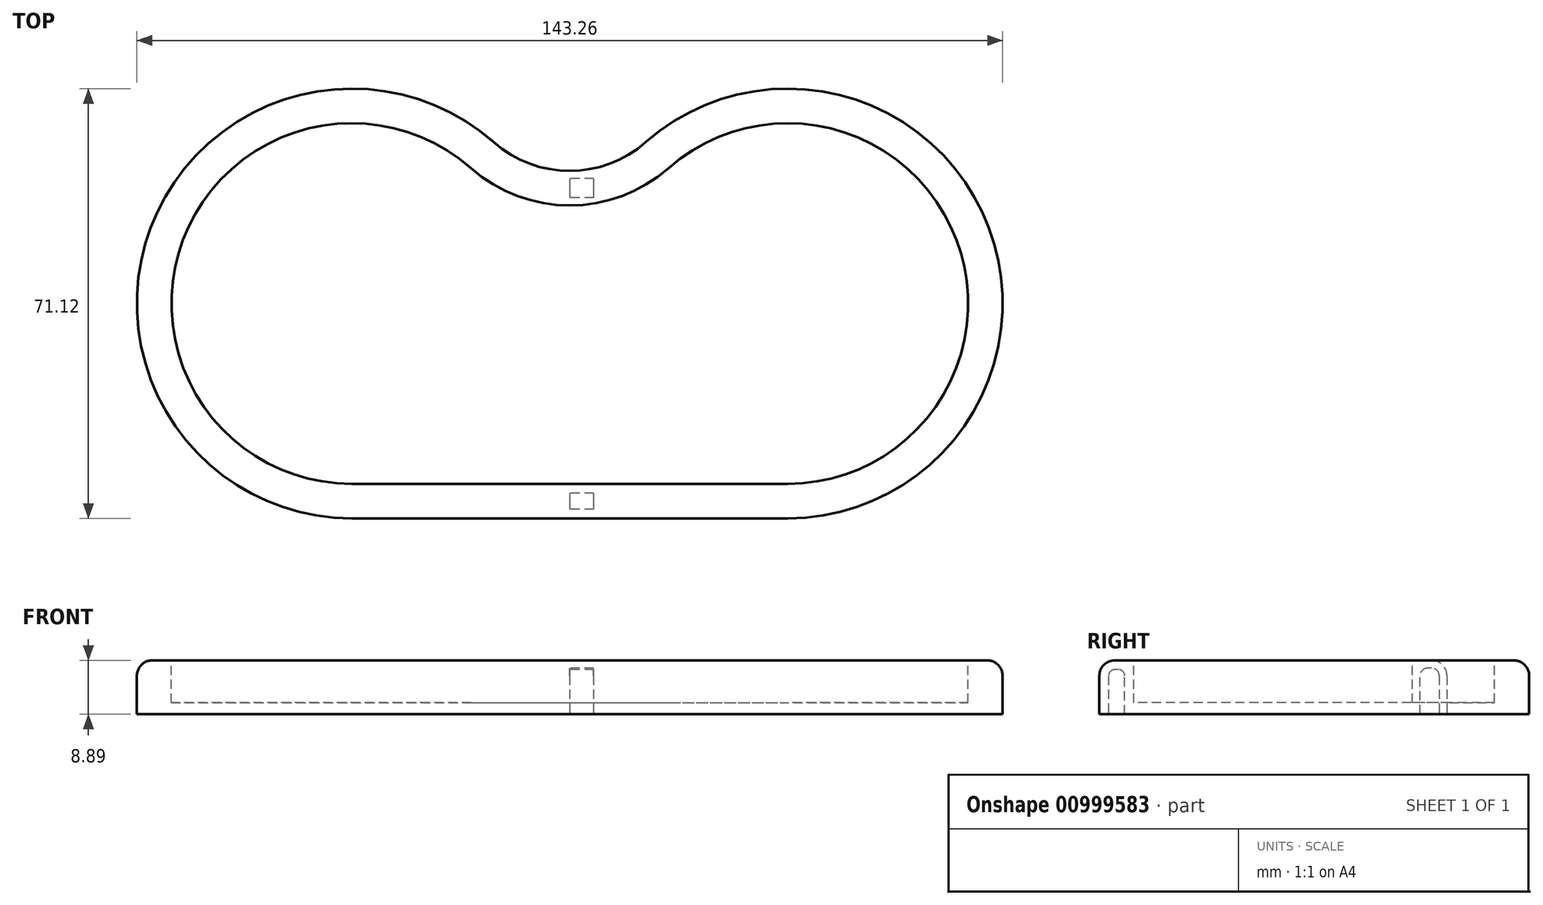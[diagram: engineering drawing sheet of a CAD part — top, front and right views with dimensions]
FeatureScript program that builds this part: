
annotation { "Feature Type Name" : "Feature", "Feature Type Description" : "" }
export const myFeature = defineFeature(function(context is Context, id is Id, definition is map)
    precondition{}
    {
        {
            var Q0;
            Q0=qCreatedBy(makeId("Top.planeOp"),FACE);
            var sketch = newSketch(context, id + "F0", { "sketchPlane" : qUnion([Q0])});
            skArc(sketch, "E0.0", {"start": v(-12.58, 29.6) * mm, "mid": v(-69.34, 15.46) * mm, "end": v(-36.07, -32.66) * mm});
            skLineSegment(sketch, "E1", {"start": v(-36.07, -32.66) * mm, "end": v(0, -32.66) * mm});
            skArc(sketch, "E2.filletArc", {"start": v(-12.58, 29.6) * mm, "mid": v(-6.72, 26.09) * mm, "end": v(0, 24.86) * mm});
            skLineSegment(sketch, "E3", {"start": v(0, 24.86) * mm, "end": v(0, -32.66) * mm});
            skSolve(sketch);
        }
        {
            var Q0;
            Q0 = qSketchRegion(id + "F0", true);
            extrude(context, id + "F1", {"entities" : qUnion([Q0]), "depth" : 8.9 * mm, "offsetDistance" : 25.4 * mm});
        }
        {
            var Q0;
            Q0=makeQuery(id+"F1.opExtrude","CAP_FACE",FACE,{"disambiguationData":[OSD([sQuery(id+"F0.wireOp",EDGE,"E0.0"),sQuery(id+"F0.wireOp",EDGE,"E1"),sQuery(id+"F0.wireOp",EDGE,"E2.filletArc"),sQuery(id+"F0.wireOp",EDGE,"E3")])],"isStart":false});
            var sketch = newSketch(context, id + "F2", { "sketchPlane" : qUnion([Q0])});
            skLineSegment(sketch, "E4.0", {"start": v(-36.07, -26.94) * mm, "end": v(0, -26.94) * mm});
            skArc(sketch, "E4.2", {"start": v(-16.36, 25.31) * mm, "mid": v(-8.74, 20.74) * mm, "end": v(0, 19.14) * mm});
            skLineSegment(sketch, "E5", {"start": v(0, 19.14) * mm, "end": v(0, -26.94) * mm});
            skArc(sketch, "E6", {"start": v(-16.36, 25.31) * mm, "mid": v(-64, 13.44) * mm, "end": v(-36.07, -26.94) * mm});
            skArc(sketch, "E7", {"start": v(-36.07, -26.94) * mm, "mid": v(-8.14, -7.63) * mm, "end": v(-16.36, 25.31) * mm, "construction": true});
            skSolve(sketch);
        }
        {
            var Q0;
            Q0 = qSketchRegion(id + "F2", true);
            extrude(context, id + "F3", {"entities" : qUnion([Q0]), "operationType" : NewBodyOperationType.REMOVE, "oppositeDirection" : true, "depth" : 7 * mm, "offsetDistance" : 25.4 * mm});
        }
        {
            var Q0;
            Q0=makeQuery(id+"F3.boolean.opBoolean","COPY",EDGE,{"derivedFrom":makeQuery(id+"F3.opExtrude","CAP_EDGE",EDGE,{"disambiguationData":[OSD([sQuery(id+"F2.wireOp",EDGE,"E4.2")])],"isStart":true})});
            var Q1;
            Q1=makeQuery(id+"F1.opExtrude","CAP_EDGE",EDGE,{"disambiguationData":[OSD([sQuery(id+"F0.wireOp",EDGE,"E2.filletArc")])],"isStart":false});
            fillet(context, id + "F4", {"entities" : qUnion([Q0, Q1]), "radius" : 2.54 * mm, "tangentPropagation" : true, "allowEdgeOverflow" : false});
        }
        {
            var Q0;
            Q0=makeQuery(id+"F1.opExtrude","SWEPT_FACE",FACE,{"disambiguationData":[OSD([sQuery(id+"F0.wireOp",EDGE,"E3")])]});
            var sketch = newSketch(context, id + "F5", { "sketchPlane" : qUnion([Q0])});
            skLineSegment(sketch, "E8.0", {"start": v(-31.13, 6.35) * mm, "end": v(-31.13, 0) * mm});
            skLineSegment(sketch, "E8.1", {"start": v(-28.46, 0) * mm, "end": v(-28.46, 6.35) * mm});
            skArc(sketch, "E8.2", {"start": v(-28.46, 6.35) * mm, "mid": v(-28.76, 7.07) * mm, "end": v(-29.48, 7.37) * mm});
            skLineSegment(sketch, "E8.3", {"start": v(-29.48, 7.37) * mm, "end": v(-30.12, 7.37) * mm});
            skArc(sketch, "E8.4", {"start": v(-30.12, 7.37) * mm, "mid": v(-30.83, 7.07) * mm, "end": v(-31.13, 6.35) * mm});
            skLineSegment(sketch, "E9", {"start": v(-31.13, 0) * mm, "end": v(-28.46, 0) * mm});
            skLineSegment(sketch, "E10.0", {"start": v(23.59, 6.35) * mm, "end": v(23.59, 0) * mm});
            skLineSegment(sketch, "E10.1", {"start": v(20.41, 0) * mm, "end": v(20.41, 6.35) * mm});
            skArc(sketch, "E10.2", {"start": v(21.68, 7.62) * mm, "mid": v(20.79, 7.25) * mm, "end": v(20.41, 6.35) * mm});
            skLineSegment(sketch, "E10.3", {"start": v(22.32, 7.62) * mm, "end": v(21.68, 7.62) * mm});
            skArc(sketch, "E10.4", {"start": v(23.59, 6.35) * mm, "mid": v(23.22, 7.25) * mm, "end": v(22.32, 7.62) * mm});
            skLineSegment(sketch, "E11", {"start": v(20.41, 0) * mm, "end": v(23.59, 0) * mm});
            skSolve(sketch);
        }
        {
            var Q0;
            Q0=makeQuery(id+"F1.opExtrude","SWEPT_BODY",BODY,{"disambiguationData":[OSD([sQuery(id+"F0.wireOp",EDGE,"E0.0"),sQuery(id+"F0.wireOp",EDGE,"E1"),sQuery(id+"F0.wireOp",EDGE,"E2.filletArc"),sQuery(id+"F0.wireOp",EDGE,"E3")])]});
            var Q1;
            Q1=qCreatedBy(makeId("Right.planeOp"),FACE);
            mirror(context, id + "F6", {"entities" : qUnion([Q0]), "mirrorPlane" : qUnion([Q1])});
        }
        {
            var Q0;
            {var subQ15=sQuery(id+"F5.wireOp",EDGE,"E8.0");Q0=makeQuery(id+"F5.imprint","IMPRINT",FACE,{"disambiguationData":[TD([[makeQuery(id+"F5.imprint","IMPRINT",EDGE,{"derivedFrom":subQ15}),-1.0]])]});}
            var sketch = newSketch(context, id + "F7", { "sketchPlane" : qUnion([Q0])});
            skArc(sketch, "E12.0", {"start": v(-30.12, 7.32) * mm, "mid": v(-30.8, 7.03) * mm, "end": v(-31.08, 6.35) * mm});
            skLineSegment(sketch, "E12.2", {"start": v(-28.52, 0) * mm, "end": v(-28.52, 6.35) * mm});
            skLineSegment(sketch, "E12.3", {"start": v(-31.08, 6.35) * mm, "end": v(-31.08, 0) * mm});
            skArc(sketch, "E12.4", {"start": v(-28.52, 6.35) * mm, "mid": v(-28.8, 7.03) * mm, "end": v(-29.48, 7.32) * mm});
            skLineSegment(sketch, "E12.5", {"start": v(-29.48, 7.32) * mm, "end": v(-30.12, 7.32) * mm});
            skLineSegment(sketch, "E13", {"start": v(-31.08, 0) * mm, "end": v(-28.52, 0) * mm});
            skLineSegment(sketch, "E14.0", {"start": v(23.54, 6.35) * mm, "end": v(23.54, 0) * mm});
            skLineSegment(sketch, "E14.1", {"start": v(20.46, 0) * mm, "end": v(20.46, 6.35) * mm});
            skArc(sketch, "E14.2", {"start": v(21.68, 7.57) * mm, "mid": v(20.82, 7.21) * mm, "end": v(20.46, 6.35) * mm});
            skLineSegment(sketch, "E14.3", {"start": v(22.32, 7.57) * mm, "end": v(21.68, 7.57) * mm});
            skArc(sketch, "E14.4", {"start": v(23.54, 6.35) * mm, "mid": v(23.18, 7.21) * mm, "end": v(22.32, 7.57) * mm});
            skLineSegment(sketch, "E15", {"start": v(20.46, 0) * mm, "end": v(23.54, 0) * mm});
            skSolve(sketch);
        }
        {
            var Q0;
            Q0 = qSketchRegion(id + "F7", true);
            extrude(context, id + "F8", {"entities" : qUnion([Q0]), "operationType" : NewBodyOperationType.ADD, "depth" : 3.8 * mm, "offsetDistance" : 25.4 * mm});
        }
        {
            var Q0;
            Q0=makeQuery(id+"F5.imprint","IMPRINT",FACE,{"disambiguationData":[TD([[makeQuery(id+"F5.imprint","IMPRINT",EDGE,{"derivedFrom":sQuery(id+"F5.wireOp",EDGE,"E10.0")}),-1.0]])]});
            var Q1;
            Q1=makeQuery(id+"F5.imprint","IMPRINT",FACE,{"disambiguationData":[TD([[makeQuery(id+"F5.imprint","IMPRINT",EDGE,{"derivedFrom":sQuery(id+"F5.wireOp",EDGE,"E8.0")}),1.0]])]});
            extrude(context, id + "F9", {"entities" : qUnion([Q0, Q1]), "operationType" : NewBodyOperationType.REMOVE, "depth" : 3.94 * mm, "offsetDistance" : 25.4 * mm});
        }
    });
